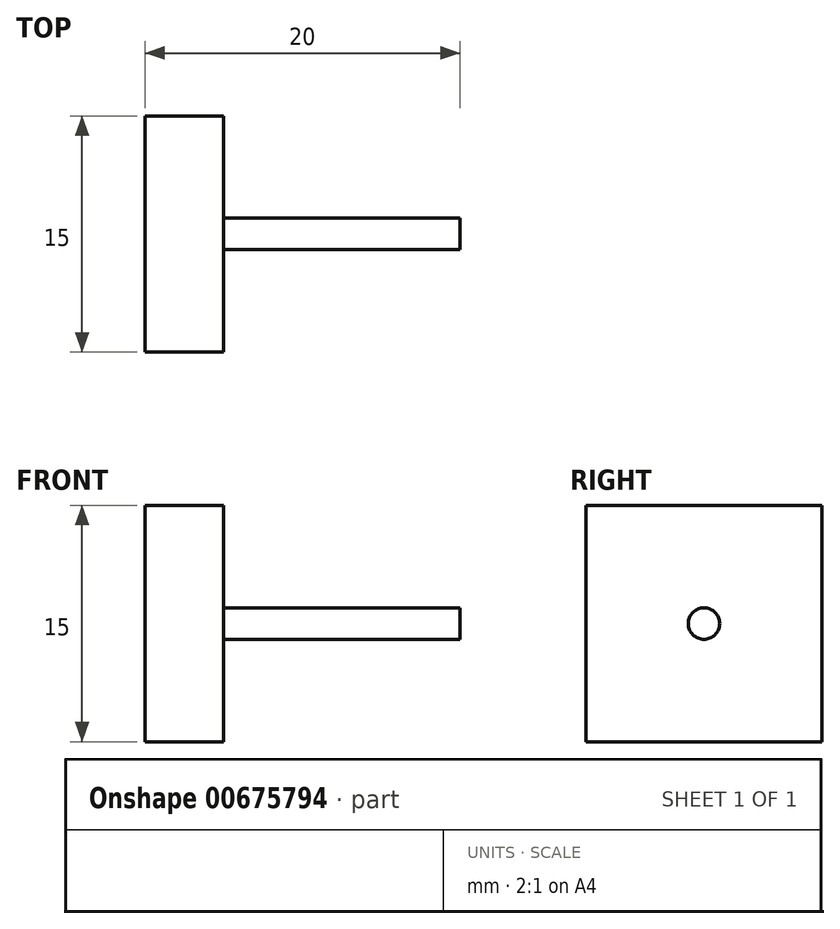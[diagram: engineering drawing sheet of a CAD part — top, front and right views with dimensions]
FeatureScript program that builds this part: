
annotation { "Feature Type Name" : "Feature", "Feature Type Description" : "" }
export const myFeature = defineFeature(function(context is Context, id is Id, definition is map)
    precondition{}
    {
        {
            var Q0;
            Q0=qCreatedBy(makeId("Right.planeOp"),FACE);
            var sketch = newSketch(context, id + "F0", { "sketchPlane" : qUnion([Q0])});
            skLineSegment(sketch, "E0.bottom", {"start": v(7.5, 7.5) * mm, "end": v(-7.5, 7.5) * mm});
            skLineSegment(sketch, "E0.top", {"start": v(7.5, -7.5) * mm, "end": v(-7.5, -7.5) * mm});
            skLineSegment(sketch, "E0.left", {"start": v(7.5, 7.5) * mm, "end": v(7.5, -7.5) * mm});
            skLineSegment(sketch, "E0.right", {"start": v(-7.5, 7.5) * mm, "end": v(-7.5, -7.5) * mm});
            skPoint(sketch, "E0.middle", {"position": v(0, 0) * mm});
            skCircle(sketch, "E1", {"center": v(0, 0) * mm, "radius": 1 * mm});
            skSolve(sketch);
        }
        {
            var Q0;
            Q0=makeQuery(id+"F0.imprint","IMPRINT",FACE,{"disambiguationData":[TD([[makeQuery(id+"F0.imprint","IMPRINT",EDGE,{"derivedFrom":sQuery(id+"F0.wireOp",EDGE,"E0.bottom")}),1.0]])]});
            extrude(context, id + "F1", {"entities" : qUnion([Q0]), "depth" : 5 * mm, "offsetDistance" : 25 * mm});
        }
        {
            var Q0;
            Q0=makeQuery(id+"F0.imprint","IMPRINT",FACE,{"disambiguationData":[TD([[makeQuery(id+"F0.imprint","IMPRINT",EDGE,{"derivedFrom":sQuery(id+"F0.wireOp",EDGE,"E1")}),1.0]])]});
            extrude(context, id + "F2", {"entities" : qUnion([Q0]), "operationType" : NewBodyOperationType.ADD, "depth" : 20 * mm, "offsetDistance" : 25 * mm});
        }
    });
